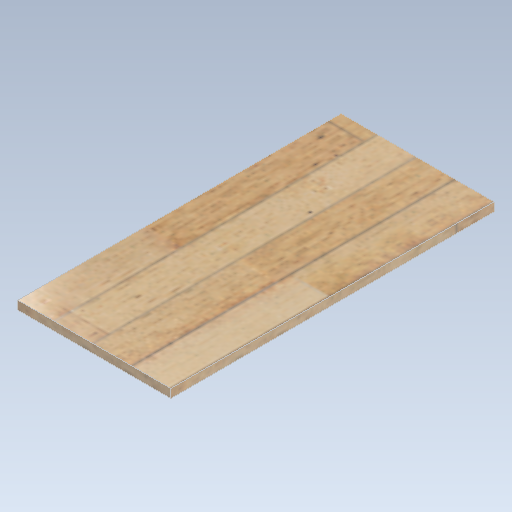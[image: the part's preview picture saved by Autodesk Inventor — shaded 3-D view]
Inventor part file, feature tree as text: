
AUTODESK INVENTOR PART (.ipt)
format: ipt  version: 2021 (Build 250183000, 183)  size: 219,136 bytes
history: native  units: mm
features: extrude x1, sketch x1
ambient origin geometry x8: Origin, YZ Plane, XZ Plane, XY Plane, X Axis, Y Axis, Z Axis, Center Point
bodies: Solid1 (feature_tree)
feature tree (2):
  extrude  "Extrusion1"  [1 undecoded]
  sketch  "Sketch1"  dims[d3=0.0mm]
note: 1 required parameter value undecoded (feature->parameter linkage not recoverable at this tier; creation-order binding heuristic only, values carry confidence <= 0.55)
